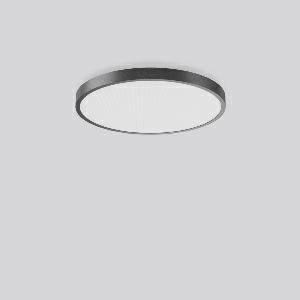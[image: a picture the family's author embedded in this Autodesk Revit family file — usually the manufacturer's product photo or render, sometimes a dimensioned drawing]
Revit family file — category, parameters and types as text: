
# Revit family: triona_round_a_312388_0031_2_76_f7bd
name_source: partatom
category: Lighting Fixtures
units: mm (PartAtom-declared; Revit-internal decimal feet)

## family parameters
Cut with Voids When Loaded = No
Host = Face
Light Source = No
Part Type = Normal
Room Calculation Point = No
Round Connector Dimension = Use Diameter
Shared = No

## types (1)
- TuneableWhite 846 (1 x LED Modul 846, 6800 lm, 4600)
    Apparent Load = 76 VA
    CIE Flux Codes = 50 80 96 73 100
    Color Rendering = 80
    Color Temperature = 4600
    Default Elevation = 1800 mm
    Description = Series: TRIONA round
Decorative round LED surface-mounted luminaire. Flat, seamless frame: aluminium extrusion profile, powder coated. Cover made of sheet steel, powder-coated. Direct light emission through a diffuser plastic opal. Indirect light emission through a flush diffuser made of satin-finish plastic. Lightguide and diffuser made of non-yellowing plastic (PMMA). Lateral light emission (RZB SIDELITE technology) for above-average homogeneous light distribution. Direct 70%, indirect 30% light emission. Tunable white versions, dynamically adjustable from 2700 K to 6500 K. Suitable for Ceiling mounting, Wall (surface). Tool-free mounting via bayonet connection. Electronic ballast included. Very easy installation thanks to Plug+Play connection. Ideal for use as part of the Human Centric Lighting concept in connection with RZB light management systems. 
Colour: anthracite metallic (DB703)
Diameter: 845 mm
Height: 88 mm
Lamp: LED
Socket: without socket
Colour temperature: 2700K - 6500K
Colour rendering index (CRI): 80
System power: 76 W
Rated luminous flux: 6800 lm
Luminous efficiency: 89 lm/W
System power 2: 78 W
Rated luminous flux 2: 6550 lm
Luminous efficiency 2: 84 lm/W
System power 3: 78 W
Rated luminous flux 3: 6550 lm
Luminous efficiency 3: 84 lm/W
Control gear: Converter, dimmable, DALI
Protection class: I
Type of protection: IP 20
    Height = 88 mm
    Lamp = 1 x LED Modul 846
    Lamp Light Flux = 6800 lm
    Lamp count = 1
    Length = 845 mm
    Lifetime = 50000 h
    Luminous efficacy = 89 lm/W
    Manufacturer = RZB
    ModVariant = No
    Model = 312388.0031.2.76
    Mounting Place = Ceiling
    Mounting Type = Surface mounted
    Number of Poles = 1
    OnlyDefault = Yes
    Power Factor = 1
    Product Name = TRIONA round A
    Product group = Surface mounted modular luminaires
    ProductGroupID = 306
    Protection Class = Protection class I
    Protection Degree = IP 20
    RLX_Detail_Level = 1
    RLX_Emergency_Light_Flux = 0 lm
    RLX_Emergency_Type = 0
    RLX_Emergency_Type_DB = No
    RlxData = <blob elided: 42441 chars, md5=efc3283a>
    Socket = socket
    Standby Power = 0 W
    System Light Flux = 6800 lm
    System Power = 76 W
    Type Comments = TuneableWhite 846
    Type Image = 312297.0031.jpg
    URL = http://relux.com
    VarID = tuneablewhite_846
    Voltage = 230 V
    Voltage Range = 220-240 V
    Weight = 0.00 kg
    Width = 0 mm  [stored 0 ft]

note: [stored X ft] marks values corroborated as IEEE doubles in the binary element streams (Revit-internal decimal feet)

## geometry (parser evidence)
native form markers: Blend x4, Sweep x13
no freeform markers — native parametric forms only
